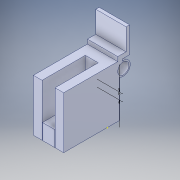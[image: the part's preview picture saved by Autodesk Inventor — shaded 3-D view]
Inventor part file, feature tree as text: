
AUTODESK INVENTOR PART (.ipt)
format: ipt  version: 2018 (Build 220112000, 112)  size: 187,392 bytes
history: native  units: in
note: dims shown in document units (in); Inventor stores cm internally (conversion verified against a paired STEP export)
features: sketch x9, extrude x5, plane x2, other x1
ambient origin geometry x8: Origin, YZ Plane, XZ Plane, XY Plane, X Axis, Y Axis, Z Axis, Center Point
bodies: Solid1 (feature_tree)
feature tree (17):
  sketch  "Sketch1"  dims[d0=0.5906in d1=0.0in d5=0.3937in]
  extrude  "Extrusion1"  Depth=0.3937in
  sketch  "Sketch3"  dims[d8=2.3622in d15=0.3937in]
  sketch  "Sketch4"  dims[d16=0.5118in d17=0.0787in]
  sketch  "Sketch8"  dims[d18=0.3937in d19=0.9843in]
  extrude  "Extrusion7"  Depth=2.3622in
  plane  "Work Plane1"
  sketch  "Sketch11"  dims[d27=1.9685in d28=0.0in]
  plane  "Work Plane2"
  extrude  "Extrusion8"  Depth=0.3937in
  extrude  "Extrusion10"  Depth=0.0787in
  sketch  "Sketch14"  dims[d31=0.5512in d32=0.0in d35=0.0787in d36=1.9685in d37=0.0in d38=0.315in d39=1.9685in d40=0.0in]
  extrude  "Extrusion11"  Depth=0.9843in
  sketch  "Sketch2"  dims[d6=0.3937in d7=2.3622in]
  sketch  "Sketch12"  dims[d29=0.7087in]
  sketch  "Sketch13"  dims[d30=0.5512in]
  other  "Boss-Extrude7"
